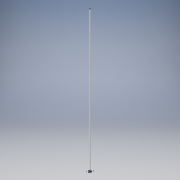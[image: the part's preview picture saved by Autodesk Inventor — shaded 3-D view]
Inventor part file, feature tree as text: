
AUTODESK INVENTOR PART (.ipt)
format: ipt  version: 2019 (Build 230136000, 136)  size: 101,376 bytes
history: native  units: mm
features: extrude x2, sketch x1, chamfer x1, mirror x1
ambient origin geometry x8: Origin, YZ Plane, XZ Plane, XY Plane, X Axis, Y Axis, Z Axis, Center Point
bodies: Solid1 (feature_tree)
feature tree (5):
  sketch  "Sketch1"  dims[d0=14.0mm d1=6.0mm d2=1000.0mm d3=0.0mm d4=50.0mm d5=0.0mm d6=1.0mm d7=2.0mm d8=45.0deg]
  extrude  "Extrusion1"  Depth=50.0mm
  extrude  "Extrusion2"  Depth=50.0mm TaperAngle=0.0deg
  chamfer  "Chamfer1"  Distance=50.0mm
  mirror  "Mirror1"
